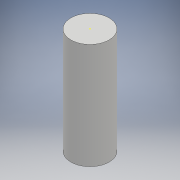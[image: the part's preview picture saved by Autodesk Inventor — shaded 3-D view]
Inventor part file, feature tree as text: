
AUTODESK INVENTOR PART (.ipt)
format: ipt  version: 2017 SP1 (Build 210196100, 196)  size: 90,112 bytes
history: native  units: mm
features: sketch x2, extrude x1
ambient origin geometry x8: Origin, YZ Plane, XZ Plane, XY Plane, X Axis, Y Axis, Z Axis, Center Point
bodies: Solide1 (feature_tree)
feature tree (3):
  extrude  "Extrusion1"  Depth=10.0mm TaperAngle=0.0deg
  sketch  "Esquisse2"
  sketch  "Esquisse1"
